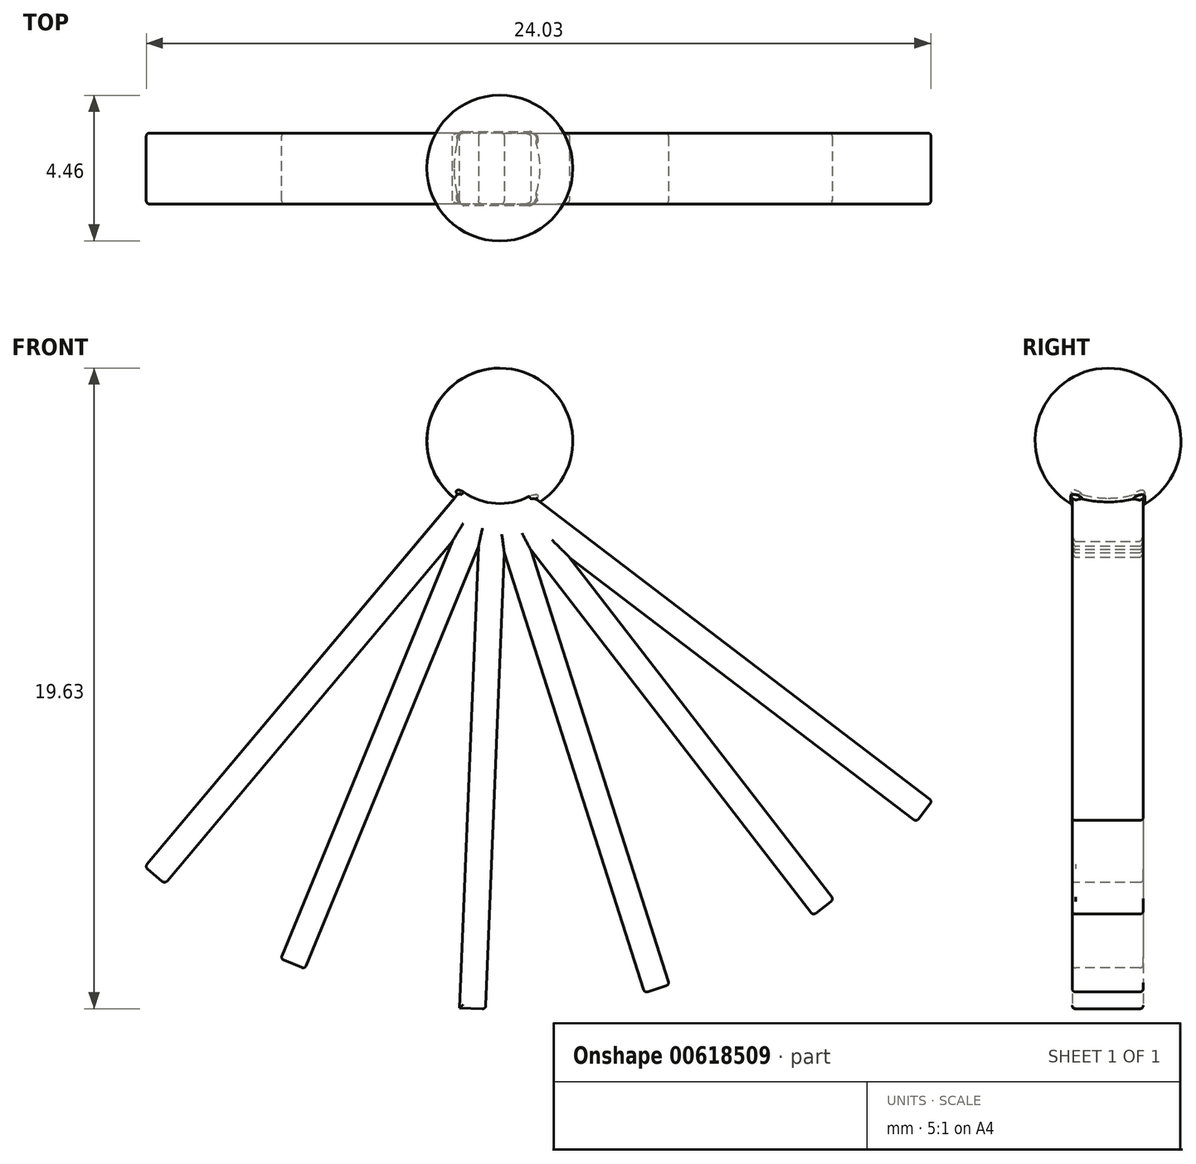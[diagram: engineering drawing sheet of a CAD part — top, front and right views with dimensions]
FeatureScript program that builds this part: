
annotation { "Feature Type Name" : "Feature", "Feature Type Description" : "" }
export const myFeature = defineFeature(function(context is Context, id is Id, definition is map)
    precondition{}
    {
        {
            var Q0;
            Q0=qCreatedBy(makeId("Right.planeOp"),FACE);
            var sketch = newSketch(context, id + "F0", { "sketchPlane" : qUnion([Q0])});
            skLineSegment(sketch, "E0.bottom", {"start": v(0, 12.17) * mm, "end": v(2.18, 12.17) * mm});
            skLineSegment(sketch, "E0.top", {"start": v(0, -3.75) * mm, "end": v(2.18, -3.75) * mm});
            skLineSegment(sketch, "E0.left", {"start": v(0, 12.17) * mm, "end": v(0, -3.75) * mm});
            skLineSegment(sketch, "E0.right", {"start": v(2.18, 12.17) * mm, "end": v(2.18, -3.75) * mm});
            skSolve(sketch);
        }
        {
            var Q0;
            Q0 = qSketchRegion(id + "F0", true);
            extrude(context, id + "F1", {"entities" : qUnion([Q0]), "depth" : .8 * mm, "offsetDistance" : 25 * mm});
        }
        {
            var Q0;
            Q0=qCreatedBy(makeId("Front.planeOp"),FACE);
            var sketch = newSketch(context, id + "F2", { "sketchPlane" : qUnion([Q0])});
            skCircle(sketch, "E1", {"center": v(6.1, 5.42) * mm, "radius": 1.86 * mm});
            skSolve(sketch);
        }
        {
            var Q0;
            Q0=makeQuery(id+"F1.opExtrude","SWEPT_BODY",BODY,{"disambiguationData":[OSD([sQuery(id+"F0.wireOp",EDGE,"E0.bottom"),sQuery(id+"F0.wireOp",EDGE,"E0.top"),sQuery(id+"F0.wireOp",EDGE,"E0.left"),sQuery(id+"F0.wireOp",EDGE,"E0.right")])]});
            var Q1;
            Q1=sQuery(id+"F2.wireOp",EDGE,"E1");
            transform(context, id + "F3", {"entities" : qUnion([Q0]), "transformType" : TransformType.ROTATION, "transformAxis" : qUnion([Q1]), "angle" : 40 * degree, "oppositeDirection" : true, "makeCopy" : false});
        }
        {
            var Q0;
            Q0=makeQuery(id+"F1.opExtrude","SWEPT_BODY",BODY,{"disambiguationData":[OSD([sQuery(id+"F0.wireOp",EDGE,"E0.bottom"),sQuery(id+"F0.wireOp",EDGE,"E0.top"),sQuery(id+"F0.wireOp",EDGE,"E0.left"),sQuery(id+"F0.wireOp",EDGE,"E0.right")])]});
            transform(context, id + "F4", {"entities" : qUnion([Q0]), "transformType" : TransformType.COPY});
        }
        {
            var Q0;
            Q0=qCreatedBy(makeId("Front.planeOp"),FACE);
            var sketch = newSketch(context, id + "F5", { "sketchPlane" : qUnion([Q0])});
            skCircle(sketch, "E2", {"center": v(6.7, 14.29) * mm, "radius": 2.67 * mm});
            skSolve(sketch);
        }
        {
            var Q0;
            Q0=makeQuery(id+"F1.opExtrude","SWEPT_BODY",BODY,{"disambiguationData":[OSD([sQuery(id+"F0.wireOp",EDGE,"E0.bottom"),sQuery(id+"F0.wireOp",EDGE,"E0.top"),sQuery(id+"F0.wireOp",EDGE,"E0.left"),sQuery(id+"F0.wireOp",EDGE,"E0.right")])]});
            var Q1;
            Q1=sQuery(id+"F5.wireOp",EDGE,"E2");
            transform(context, id + "F6", {"entities" : qUnion([Q0]), "transformType" : TransformType.ROTATION, "transformAxis" : qUnion([Q1]), "angle" : 17.67 * degree, "makeCopy" : false});
        }
        {
            var Q0;
            Q0=makeQuery(id+"F1.opExtrude","SWEPT_BODY",BODY,{"disambiguationData":[OSD([sQuery(id+"F0.wireOp",EDGE,"E0.bottom"),sQuery(id+"F0.wireOp",EDGE,"E0.top"),sQuery(id+"F0.wireOp",EDGE,"E0.left"),sQuery(id+"F0.wireOp",EDGE,"E0.right")])]});
            transform(context, id + "F7", {"entities" : qUnion([Q0]), "transformType" : TransformType.COPY});
        }
        {
            var Q0;
            Q0=makeQuery(id+"F1.opExtrude","SWEPT_BODY",BODY,{"disambiguationData":[OSD([sQuery(id+"F0.wireOp",EDGE,"E0.bottom"),sQuery(id+"F0.wireOp",EDGE,"E0.top"),sQuery(id+"F0.wireOp",EDGE,"E0.left"),sQuery(id+"F0.wireOp",EDGE,"E0.right")])]});
            var Q1;
            Q1=sQuery(id+"F5.wireOp",EDGE,"E2");
            transform(context, id + "F8", {"entities" : qUnion([Q0]), "transformType" : TransformType.ROTATION, "transformAxis" : qUnion([Q1]), "angle" : 20 * degree, "makeCopy" : false});
        }
        {
            var Q0;
            Q0=makeQuery(id+"F1.opExtrude","SWEPT_BODY",BODY,{"disambiguationData":[OSD([sQuery(id+"F0.wireOp",EDGE,"E0.bottom"),sQuery(id+"F0.wireOp",EDGE,"E0.top"),sQuery(id+"F0.wireOp",EDGE,"E0.left"),sQuery(id+"F0.wireOp",EDGE,"E0.right")])]});
            transform(context, id + "F9", {"entities" : qUnion([Q0]), "transformType" : TransformType.COPY});
        }
        {
            var Q0;
            Q0=makeQuery(id+"F1.opExtrude","SWEPT_BODY",BODY,{"disambiguationData":[OSD([sQuery(id+"F0.wireOp",EDGE,"E0.bottom"),sQuery(id+"F0.wireOp",EDGE,"E0.top"),sQuery(id+"F0.wireOp",EDGE,"E0.left"),sQuery(id+"F0.wireOp",EDGE,"E0.right")])]});
            var Q1;
            Q1=sQuery(id+"F5.wireOp",EDGE,"E2");
            transform(context, id + "F10", {"entities" : qUnion([Q0]), "transformType" : TransformType.ROTATION, "transformAxis" : qUnion([Q1]), "angle" : 20 * degree, "makeCopy" : false});
        }
        {
            var Q0;
            Q0=makeQuery(id+"F1.opExtrude","SWEPT_BODY",BODY,{"disambiguationData":[OSD([sQuery(id+"F0.wireOp",EDGE,"E0.bottom"),sQuery(id+"F0.wireOp",EDGE,"E0.top"),sQuery(id+"F0.wireOp",EDGE,"E0.left"),sQuery(id+"F0.wireOp",EDGE,"E0.right")])]});
            transform(context, id + "F11", {"entities" : qUnion([Q0]), "transformType" : TransformType.COPY});
        }
        {
            var Q0;
            Q0=makeQuery(id+"F1.opExtrude","SWEPT_BODY",BODY,{"disambiguationData":[OSD([sQuery(id+"F0.wireOp",EDGE,"E0.bottom"),sQuery(id+"F0.wireOp",EDGE,"E0.top"),sQuery(id+"F0.wireOp",EDGE,"E0.left"),sQuery(id+"F0.wireOp",EDGE,"E0.right")])]});
            var Q1;
            Q1=sQuery(id+"F5.wireOp",EDGE,"E2");
            transform(context, id + "F12", {"entities" : qUnion([Q0]), "transformType" : TransformType.ROTATION, "transformAxis" : qUnion([Q1]), "angle" : 20 * degree, "makeCopy" : false});
        }
        {
            var Q0;
            Q0=makeQuery(id+"F1.opExtrude","SWEPT_BODY",BODY,{"disambiguationData":[OSD([sQuery(id+"F0.wireOp",EDGE,"E0.bottom"),sQuery(id+"F0.wireOp",EDGE,"E0.top"),sQuery(id+"F0.wireOp",EDGE,"E0.left"),sQuery(id+"F0.wireOp",EDGE,"E0.right")])]});
            transform(context, id + "F13", {"entities" : qUnion([Q0]), "transformType" : TransformType.COPY});
        }
        {
            var Q0;
            Q0=makeQuery(id+"F1.opExtrude","SWEPT_BODY",BODY,{"disambiguationData":[OSD([sQuery(id+"F0.wireOp",EDGE,"E0.bottom"),sQuery(id+"F0.wireOp",EDGE,"E0.top"),sQuery(id+"F0.wireOp",EDGE,"E0.left"),sQuery(id+"F0.wireOp",EDGE,"E0.right")])]});
            var Q1;
            Q1=sQuery(id+"F5.wireOp",EDGE,"E2");
            transform(context, id + "F14", {"entities" : qUnion([Q0]), "transformType" : TransformType.ROTATION, "transformAxis" : qUnion([Q1]), "angle" : 15 * degree, "makeCopy" : false});
        }
        {
            var Q0;
            Q0=qCreatedBy(makeId("Front.planeOp"),FACE);
            var sketch = newSketch(context, id + "F15", { "sketchPlane" : qUnion([Q0])});
            skLineSegment(sketch, "E3", {"start": v(6.6, 11.6) * mm, "end": v(6.6, 16.92) * mm});
            skCircle(sketch, "E4", {"center": v(6.6, 14.27) * mm, "radius": 2.23 * mm});
            skSolve(sketch);
        }
        {
            var Q0;
            {var subQ0=sQuery(id+"F15.wireOp",EDGE,"E4");var subQ1=sQuery(id+"F15.wireOp",EDGE,"E3");var subQ2=makeQuery(id+"F15.imprint","INTERSECT",VERTEX,{"disambiguationData":[OD(0.0)],"derivedFrom":[subQ1,subQ0]});Q0=makeQuery(id+"F15.imprint","IMPRINT",FACE,{"disambiguationData":[TD([[makeQuery(id+"F15.imprint","IMPRINT",EDGE,{"disambiguationData":[TD([[subQ2,-1.0]])],"derivedFrom":subQ1}),-1.0]])]});}
            var Q1;
            Q1=sQuery(id+"F15.wireOp",EDGE,"E3");
            revolve(context, id + "F16", {"entities" : qUnion([Q0]), "axis" : qUnion([Q1]), "revolveType" : RevolveType.FULL});
        }
        {
            var Q0;
            Q0=makeQuery(id+"F16.opRevolve","SWEPT_BODY",BODY,{"disambiguationData":[OSD([sQuery(id+"F15.wireOp",EDGE,"E3"),sQuery(id+"F15.wireOp",EDGE,"E4")])]});
            transform(context, id + "F17", {"entities" : qUnion([Q0]), "transformType" : TransformType.TRANSLATION_3D, "dx" : -0.2 * mm, "dy" : 1.1 * mm, "dz" : 1.1 * mm, "makeCopy" : false});
        }
        {
            var Q0;
            Q0=makeQuery(id+"F7.opPattern","COPY",BODY,{"derivedFrom":makeQuery(id+"F1.opExtrude","SWEPT_BODY",BODY,{"disambiguationData":[OSD([sQuery(id+"F0.wireOp",EDGE,"E0.bottom"),sQuery(id+"F0.wireOp",EDGE,"E0.top"),sQuery(id+"F0.wireOp",EDGE,"E0.left"),sQuery(id+"F0.wireOp",EDGE,"E0.right")])]}),"instanceName":"1"});
            var Q1;
            Q1=makeQuery(id+"F9.opPattern","COPY",BODY,{"derivedFrom":makeQuery(id+"F1.opExtrude","SWEPT_BODY",BODY,{"disambiguationData":[OSD([sQuery(id+"F0.wireOp",EDGE,"E0.bottom"),sQuery(id+"F0.wireOp",EDGE,"E0.top"),sQuery(id+"F0.wireOp",EDGE,"E0.left"),sQuery(id+"F0.wireOp",EDGE,"E0.right")])]}),"instanceName":"1"});
            var Q2;
            Q2=makeQuery(id+"F11.opPattern","COPY",BODY,{"derivedFrom":makeQuery(id+"F1.opExtrude","SWEPT_BODY",BODY,{"disambiguationData":[OSD([sQuery(id+"F0.wireOp",EDGE,"E0.bottom"),sQuery(id+"F0.wireOp",EDGE,"E0.top"),sQuery(id+"F0.wireOp",EDGE,"E0.left"),sQuery(id+"F0.wireOp",EDGE,"E0.right")])]}),"instanceName":"1"});
            var Q3;
            Q3=makeQuery(id+"F13.opPattern","COPY",BODY,{"derivedFrom":makeQuery(id+"F1.opExtrude","SWEPT_BODY",BODY,{"disambiguationData":[OSD([sQuery(id+"F0.wireOp",EDGE,"E0.bottom"),sQuery(id+"F0.wireOp",EDGE,"E0.top"),sQuery(id+"F0.wireOp",EDGE,"E0.left"),sQuery(id+"F0.wireOp",EDGE,"E0.right")])]}),"instanceName":"1"});
            var Q4;
            Q4=makeQuery(id+"F1.opExtrude","SWEPT_BODY",BODY,{"disambiguationData":[OSD([sQuery(id+"F0.wireOp",EDGE,"E0.bottom"),sQuery(id+"F0.wireOp",EDGE,"E0.top"),sQuery(id+"F0.wireOp",EDGE,"E0.left"),sQuery(id+"F0.wireOp",EDGE,"E0.right")])]});
            var Q5;
            Q5=makeQuery(id+"F4.opPattern","COPY",BODY,{"derivedFrom":makeQuery(id+"F1.opExtrude","SWEPT_BODY",BODY,{"disambiguationData":[OSD([sQuery(id+"F0.wireOp",EDGE,"E0.bottom"),sQuery(id+"F0.wireOp",EDGE,"E0.top"),sQuery(id+"F0.wireOp",EDGE,"E0.left"),sQuery(id+"F0.wireOp",EDGE,"E0.right")])]}),"instanceName":"1"});
            var Q6;
            Q6=makeQuery(id+"F16.opRevolve","SWEPT_BODY",BODY,{"disambiguationData":[OSD([sQuery(id+"F15.wireOp",EDGE,"E3"),sQuery(id+"F15.wireOp",EDGE,"E4")])]});
            booleanBodies(context, id + "F18", {"operationType" : BooleanOperationType.UNION, "tools" : qUnion([Q0, Q1, Q2, Q3, Q4, Q5, Q6])});
        }
        {
            var Q0;
            {var subQ0=makeQuery(id+"F1.opExtrude","SWEPT_FACE",FACE,{"disambiguationData":[OSD([sQuery(id+"F0.wireOp",EDGE,"E0.left")])]});Q0=makeQuery(id+"F18.opBoolean","MERGE",FACE,{"derivedFrom":[subQ0,makeQuery(id+"F4.opPattern","COPY",FACE,{"derivedFrom":subQ0,"instanceName":"1"}),makeQuery(id+"F7.opPattern","COPY",FACE,{"derivedFrom":subQ0,"instanceName":"1"}),makeQuery(id+"F9.opPattern","COPY",FACE,{"derivedFrom":subQ0,"instanceName":"1"}),makeQuery(id+"F11.opPattern","COPY",FACE,{"derivedFrom":subQ0,"instanceName":"1"}),makeQuery(id+"F13.opPattern","COPY",FACE,{"derivedFrom":subQ0,"instanceName":"1"})]});}
            var Q1;
            {var subQ0=makeQuery(id+"F1.opExtrude","SWEPT_FACE",FACE,{"disambiguationData":[OSD([sQuery(id+"F0.wireOp",EDGE,"E0.right")])]});Q1=makeQuery(id+"F18.opBoolean","MERGE",FACE,{"derivedFrom":[subQ0,makeQuery(id+"F4.opPattern","COPY",FACE,{"derivedFrom":subQ0,"instanceName":"1"}),makeQuery(id+"F7.opPattern","COPY",FACE,{"derivedFrom":subQ0,"instanceName":"1"}),makeQuery(id+"F9.opPattern","COPY",FACE,{"derivedFrom":subQ0,"instanceName":"1"}),makeQuery(id+"F11.opPattern","COPY",FACE,{"derivedFrom":subQ0,"instanceName":"1"}),makeQuery(id+"F13.opPattern","COPY",FACE,{"derivedFrom":subQ0,"instanceName":"1"})]});}
            var Q2;
            Q2=makeQuery(id+"F4.opPattern","COPY",FACE,{"derivedFrom":makeQuery(id+"F1.opExtrude","SWEPT_FACE",FACE,{"disambiguationData":[OSD([sQuery(id+"F0.wireOp",EDGE,"E0.top")])]}),"instanceName":"1"});
            var Q3;
            Q3=makeQuery(id+"F7.opPattern","COPY",FACE,{"derivedFrom":makeQuery(id+"F1.opExtrude","SWEPT_FACE",FACE,{"disambiguationData":[OSD([sQuery(id+"F0.wireOp",EDGE,"E0.top")])]}),"instanceName":"1"});
            var Q4;
            Q4=makeQuery(id+"F9.opPattern","COPY",EDGE,{"derivedFrom":makeQuery(id+"F1.opExtrude","CAP_EDGE",EDGE,{"disambiguationData":[OSD([sQuery(id+"F0.wireOp",EDGE,"E0.top")])],"isStart":false}),"instanceName":"1"});
            var Q5;
            Q5=makeQuery(id+"F11.opPattern","COPY",FACE,{"derivedFrom":makeQuery(id+"F1.opExtrude","SWEPT_FACE",FACE,{"disambiguationData":[OSD([sQuery(id+"F0.wireOp",EDGE,"E0.top")])]}),"instanceName":"1"});
            var Q6;
            Q6=makeQuery(id+"F13.opPattern","COPY",FACE,{"derivedFrom":makeQuery(id+"F1.opExtrude","SWEPT_FACE",FACE,{"disambiguationData":[OSD([sQuery(id+"F0.wireOp",EDGE,"E0.top")])]}),"instanceName":"1"});
            var Q7;
            Q7=makeQuery(id+"F1.opExtrude","SWEPT_FACE",FACE,{"disambiguationData":[OSD([sQuery(id+"F0.wireOp",EDGE,"E0.top")])]});
            fillet(context, id + "F19", {"entities" : qUnion([Q0, Q1, Q2, Q3, Q4, Q5, Q6, Q7]), "radius" : .1 * mm, "tangentPropagation" : true, "allowEdgeOverflow" : false});
        }
    });
